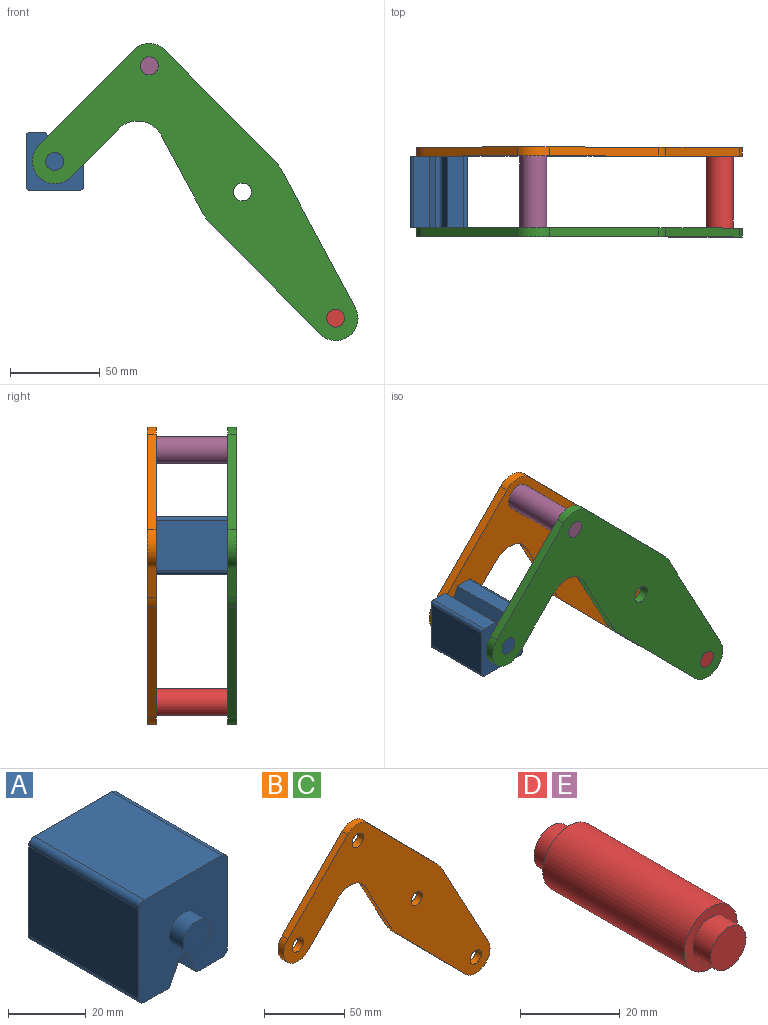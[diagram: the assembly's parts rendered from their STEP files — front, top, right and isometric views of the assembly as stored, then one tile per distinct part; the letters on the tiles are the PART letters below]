
ASSEMBLY  parts=5 mates=3
PART A: 18 faces, bbox 32.1x50x32.1 mm
  f0: plane 40x28.08mm, normal (1,0,0), area 1123.1mm2, adj f4,f10,f13,f14
  f1: plane 40x9.04mm, normal (0,0,-1), area 361.6mm2, adj f2,f4,f10,f14
  f2: plane 40x6.42mm, normal (-0.89,0,-0.45), area 287.2mm2, adj f1,f4,f10,f15
  f3: plane 40x6.42mm, normal (0.89,0,-0.45), area 287.2mm2, adj f4,f5,f10,f15
  f4: plane 32.08x32.08mm, normal (0,-1,0), area 900.6mm2, adj f0,f1,f2,f3,f5,f6,f7,f9
  f5: plane 40x9.04mm, normal (0,0,-1), area 361.6mm2, adj f3,f4,f10,f16
  f6: plane 40x28.08mm, normal (0,0,1), area 1123.1mm2, adj f4,f10,f13,f17
  f7: plane 40x28.08mm, normal (-1,0,0), area 1123.1mm2, adj f4,f10,f16,f17
  f8: plane 10x10mm, normal (0,-1,0), area 78.5mm2, adj f9
  f9: cylinder r=5mm len=10mm, axis (0,1,0), area 157.1mm2, adj f4,f8
  f10: plane 32.08x32.08mm, normal (0,1,0), area 900.6mm2, adj f0,f1,f2,f3,f5,f6,f7,f12
  f11: plane 10x10mm, normal (0,1,0), area 78.5mm2, adj f12
  f12: cylinder r=5mm len=10mm, axis (0,-1,0), area 157.1mm2, adj f10,f11
  f13: cylinder r=2mm len=40mm, axis (0,1,0), area 125.7mm2, adj f0,f4,f6,f10
  f14: cylinder r=2mm len=40mm, axis (0,-1,0), area 125.7mm2, adj f0,f1,f4,f10
  f15: cylinder r=2mm len=40mm, axis (0,1,0), area 177.1mm2, adj f2,f3,f4,f10
  f16: cylinder r=2mm len=40mm, axis (0,1,0), area 125.7mm2, adj f4,f5,f7,f10
  f17: cylinder r=2mm len=40mm, axis (0,-1,0), area 125.7mm2, adj f4,f6,f7,f10
PART B: 18 faces, bbox 181.7x5x165.8 mm
  f0: plane 43.49x23.35mm, normal (-0.88,0,-0.47), area 246.8mm2, adj f1,f14,f16,f17
  f1: cylinder r=25mm len=5.75mm, axis (0,1,0), area 35.8mm2, adj f0,f2,f16,f17
  f2: plane 61.6x60.87mm, normal (-0.71,0,-0.7), area 433mm2, adj f1,f3,f16,f17
  f3: cylinder r=12.5mm len=21.39mm, axis (0,1,0), area 178.4mm2, adj f2,f4,f16,f17
  f4: plane 76.3x40.96mm, normal (0.88,0,0.47), area 433mm2, adj f3,f5,f16,f17
  f5: cylinder r=25mm len=5.75mm, axis (0,1,0), area 35.8mm2, adj f4,f6,f16,f17
  f6: plane 61.6x60.87mm, normal (0.71,0,0.7), area 433mm2, adj f5,f7,f16,f17
  f7: cylinder r=12.5mm len=17.78mm, axis (0,1,0), area 98.9mm2, adj f6,f8,f16,f17
  f8: plane 53.35x52.71mm, normal (-0.71,0,0.7), area 375mm2, adj f7,f9,f16,f17
  f9: cylinder r=12.5mm len=21.39mm, axis (0,1,0), area 196.3mm2, adj f8,f10,f16,f17
  f10: plane 26.86x26.54mm, normal (0.71,0,-0.7), area 188.8mm2, adj f9,f14,f16,f17
  f11: cylinder r=5mm len=10mm, axis (0,1,0), area 157.1mm2, adj f16,f17
  f12: cylinder r=5mm len=10mm, axis (0,1,0), area 157.1mm2, adj f16,f17
  f13: cylinder r=5mm len=10mm, axis (0,1,0), area 157.1mm2, adj f16,f17
  f14: cylinder r=15mm len=23.89mm, axis (0,1,0), area 140.2mm2, adj f0,f10,f16,f17
  f15: cylinder r=5mm len=10mm, axis (0,1,0), area 157.1mm2, adj f16,f17
  f16: plane 181.66x165.78mm, normal (0,-1,0), area 8710.1mm2, adj f0,f1,f2,f3,f4,f5,f6,f7
  f17: plane 181.66x165.78mm, normal (0,1,0), area 8710.1mm2, adj f0,f1,f2,f3,f4,f5,f6,f7
PART C: same geometry as B
PART D: 7 faces, bbox 15x50x15 mm
  f0: cylinder r=7.5mm len=40mm, axis (0,-1,0), area 1885mm2, adj f2,f5
  f1: cylinder r=5mm len=10mm, axis (0,1,0), area 157.1mm2, adj f2,f3
  f2: plane 15x15mm, normal (0,-1,0), area 98.2mm2, adj f0,f1
  f3: plane 10x10mm, normal (0,-1,0), area 78.5mm2, adj f1
  f4: cylinder r=5mm len=10mm, axis (0,-1,0), area 157.1mm2, adj f5,f6
  f5: plane 15x15mm, normal (0,1,0), area 98.2mm2, adj f0,f4
  f6: plane 10x10mm, normal (0,1,0), area 78.5mm2, adj f4
PART E: same geometry as D
PLACE A rot(axis=(1,0,0),180deg) t=(0,20,34.08)mm
PLACE B t=(0,25,0)mm
PLACE C t=(0,-20,0)mm fixed
PLACE D rot(axis=(1,0,0),180deg) t=(103.95,20,0)mm
PLACE E t=(0,-20,0)mm
MATE revolute A.f9 <-> C.f9  axis (0,1,0) through (-104.69,-20,17.04)mm
MATE fastened C.f3 <-> D.f0  axis (0,1,0) through (51.98,-20,-70.39)mm
MATE fastened E.f0 <-> B.f7  axis (0,1,0) through (-51.98,20,70.39)mm
